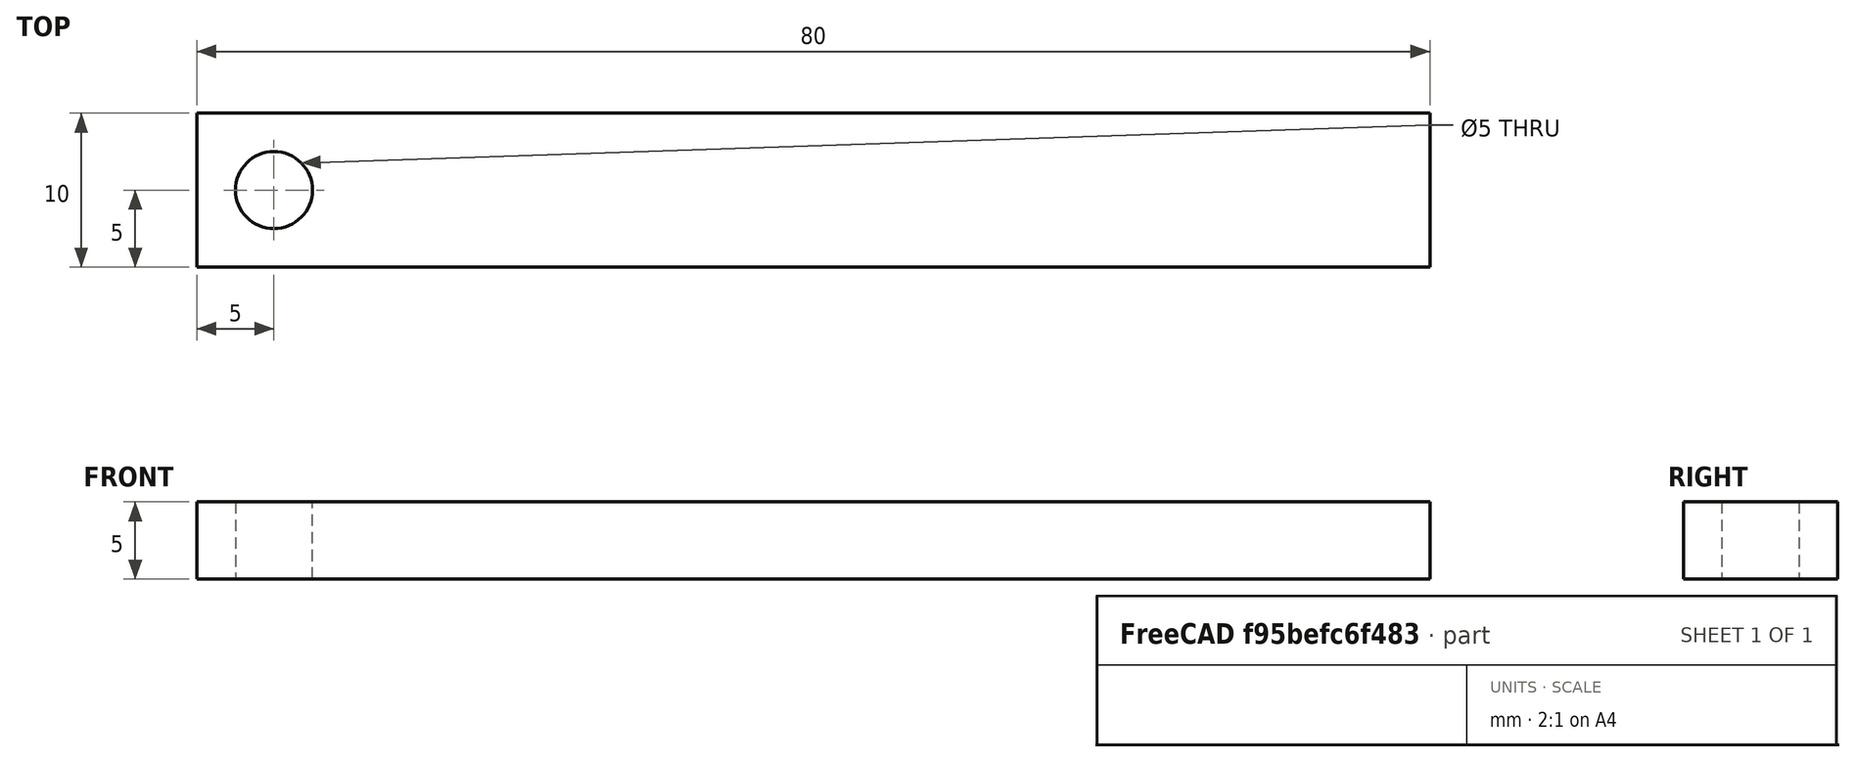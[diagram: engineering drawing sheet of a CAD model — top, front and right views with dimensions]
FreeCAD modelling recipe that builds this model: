
FCSTD DOCUMENT  (FreeCAD 0.21RUnknown)
Label: part16_rectange
License: All rights reserved
LicenseURL: http://en.wikipedia.org/wiki/All_rights_reserved
objects: Sketcher::SketchObject×1, Part::Extrusion×1, PartDesign::Line×1, App::Part×1
note: 3 computed .brp shape members not serialized (recipe doc carries the construction recipe); baked Part::Feature solids carry a one-line shape summary decoded from their .brp

FEATURE [Sketcher::SketchObject] Sketch
  FullyConstrained = true
  sketch-geometry (5):
    g0: LineSegment StartX=-40 StartY=5 StartZ=0 EndX=40 EndY=5 EndZ=0
    g1: LineSegment StartX=40 StartY=5 StartZ=0 EndX=40 EndY=-5 EndZ=0
    g2: LineSegment StartX=40 StartY=-5 StartZ=0 EndX=-40 EndY=-5 EndZ=0
    g3: LineSegment StartX=-40 StartY=-5 StartZ=0 EndX=-40 EndY=5 EndZ=0
    g4: Circle CenterX=-35 CenterY=0 CenterZ=0 NormalX=0 NormalY=0 NormalZ=1 AngleXU=0 Radius=2.5
  constraints (14):
    c: Coincident(g0,g1)
    c: Coincident(g1,g2)
    c: Coincident(g2,g3)
    c: Coincident(g3,g0)
    c: Horizontal(g0)
    c: Horizontal(g2)
    c: Vertical(g1)
    c: Vertical(g3)
    c: Symmetric(g2,g0,g-1)
    c: DistanceX(g0,g0) = 80
    c: DistanceY(g2,g0) = 10
    c: PointOnObject(g4,g-1)
    c: Diameter(g4) = 5
    c: DistanceX(g0,g4) = 5
FEATURE [Part::Extrusion] Extrude
  Base = -> Sketch
  Dir = (0,0,1)
  DirMode = 2
  FaceMakerClass = Part::FaceMakerBullseye
  LengthFwd = 5
  LengthRev = 0
  Solid = true
  Symmetric = false
FEATURE [PartDesign::Line] HoleAxis_1
  AttacherType = Attacher::AttachEngineLine
  Length = 7.04534
  MapMode = 19
  Placement = pos=(-35,0,5) rot=(0,0,1;0rad)
  ResizeMode = 1
  Support = -> [Extrude]
FEATURE [App::Part] Part  label="rectangle"
  Group = -> [Sketch,Extrude,HoleAxis_1]
  Origin = -> Origin
